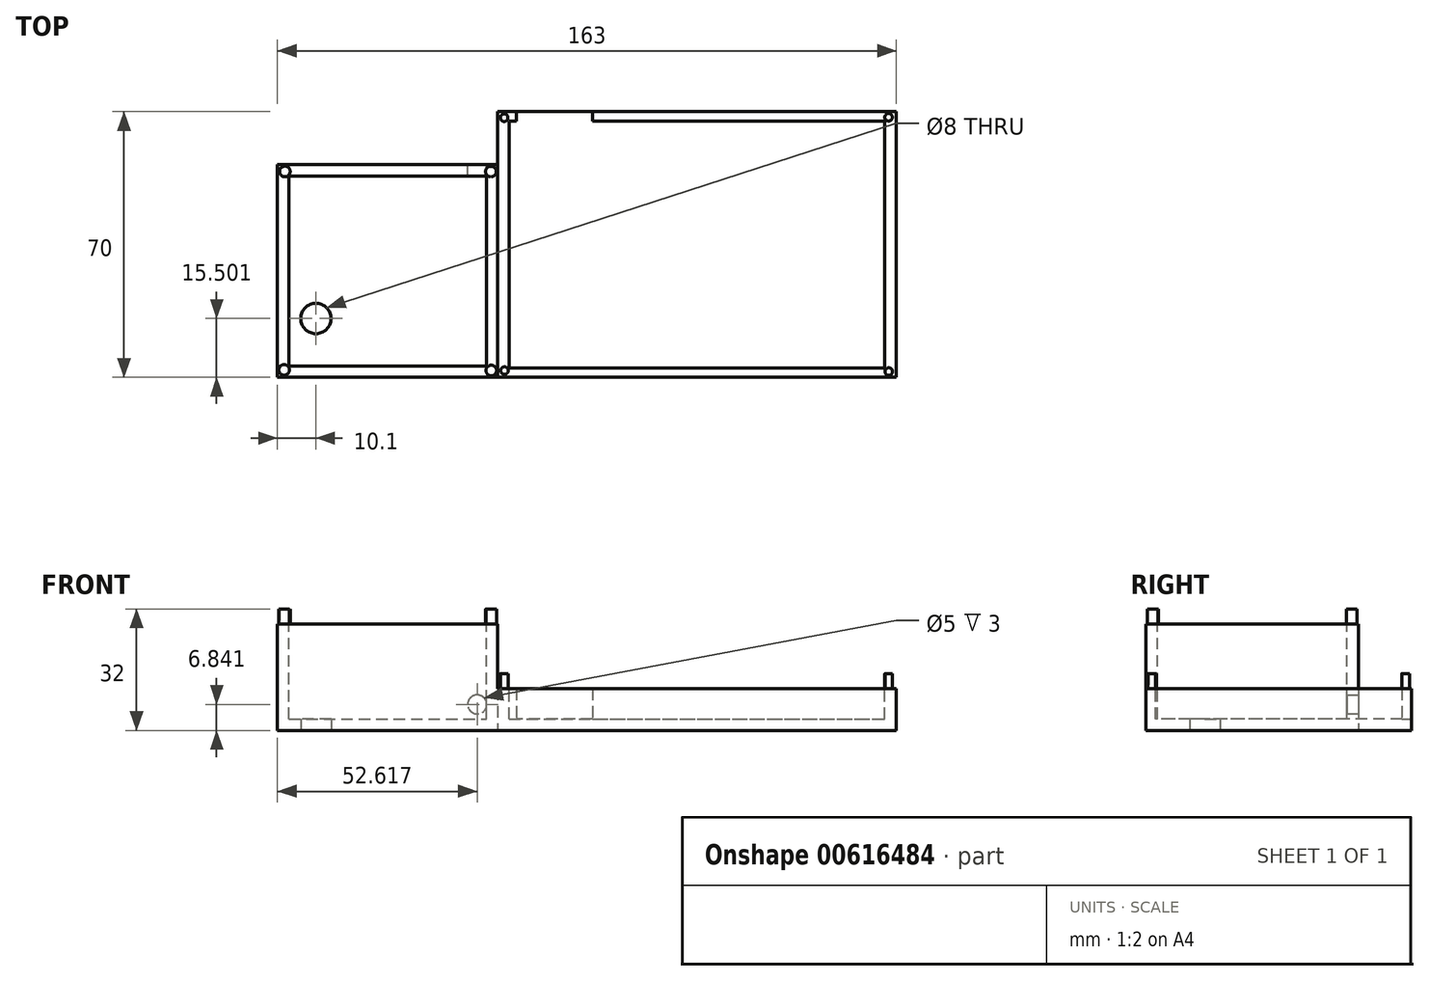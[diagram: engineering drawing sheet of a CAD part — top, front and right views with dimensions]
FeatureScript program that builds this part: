
annotation { "Feature Type Name" : "Feature", "Feature Type Description" : "" }
export const myFeature = defineFeature(function(context is Context, id is Id, definition is map)
    precondition{}
    {
        {
            var Q0;
            Q0=qCreatedBy(makeId("Top.planeOp"),FACE);
            var sketch = newSketch(context, id + "F0", { "sketchPlane" : qUnion([Q0])});
            skLineSegment(sketch, "E0.bottom", {"start": v(-52.5, 35) * mm, "end": v(52.5, 35) * mm});
            skLineSegment(sketch, "E0.top", {"start": v(-52.5, -35) * mm, "end": v(52.5, -35) * mm});
            skLineSegment(sketch, "E0.left", {"start": v(-52.5, 35) * mm, "end": v(-52.5, -35) * mm});
            skLineSegment(sketch, "E0.right", {"start": v(52.5, 35) * mm, "end": v(52.5, -35) * mm});
            skPoint(sketch, "E0.middle", {"position": v(0, 0) * mm});
            skSolve(sketch);
        }
        {
            var Q0;
            Q0=qCreatedBy(makeId("Top.planeOp"),FACE);
            var sketch = newSketch(context, id + "F1", { "sketchPlane" : qUnion([Q0])});
            skLineSegment(sketch, "E1.bottom", {"start": v(-52.5, 21) * mm, "end": v(-110.5, 21) * mm});
            skLineSegment(sketch, "E1.top", {"start": v(-52.5, -35) * mm, "end": v(-110.5, -35) * mm});
            skLineSegment(sketch, "E1.left", {"start": v(-52.5, 21) * mm, "end": v(-52.5, -35) * mm});
            skLineSegment(sketch, "E1.right", {"start": v(-110.5, 21) * mm, "end": v(-110.5, -35) * mm});
            skSolve(sketch);
        }
        {
            var Q0;
            Q0=makeQuery(id+"F1.imprint","IMPRINT",FACE,{"disambiguationData":[TD([[makeQuery(id+"F1.imprint","IMPRINT",EDGE,{"derivedFrom":sQuery(id+"F1.wireOp",EDGE,"E1.bottom")}),1.0]])]});
            var Q1;
            Q1=makeQuery(id+"F0.imprint","IMPRINT",FACE,{"disambiguationData":[TD([[makeQuery(id+"F0.imprint","IMPRINT",EDGE,{"derivedFrom":sQuery(id+"F0.wireOp",EDGE,"E0.bottom")}),-1.0]])]});
            extrude(context, id + "F2", {"entities" : qUnion([Q0, Q1]), "depth" : 11 * mm, "offsetDistance" : 25 * mm});
        }
        {
            var Q0;
            Q0=makeQuery(id+"F2.opExtrude","CAP_FACE",FACE,{"disambiguationData":[OSD([sQuery(id+"F0.wireOp",EDGE,"E0.bottom"),sQuery(id+"F0.wireOp",EDGE,"E0.top"),sQuery(id+"F0.wireOp",EDGE,"E0.left"),sQuery(id+"F0.wireOp",EDGE,"E0.right")])],"isStart":false});
            var sketch = newSketch(context, id + "F3", { "sketchPlane" : qUnion([Q0])});
            skLineSegment(sketch, "E2.bottom", {"start": v(-49.5, 32.5) * mm, "end": v(49.5, 32.5) * mm});
            skLineSegment(sketch, "E2.top", {"start": v(-49.5, -32.5) * mm, "end": v(49.5, -32.5) * mm});
            skLineSegment(sketch, "E2.left", {"start": v(-49.5, 32.5) * mm, "end": v(-49.5, -32.5) * mm});
            skLineSegment(sketch, "E2.right", {"start": v(49.5, 32.5) * mm, "end": v(49.5, -32.5) * mm});
            skPoint(sketch, "E2.middle", {"position": v(0, 0) * mm});
            skSolve(sketch);
        }
        {
            var Q0;
            Q0=makeQuery(id+"F3.imprint","IMPRINT",FACE,{"disambiguationData":[TD([[makeQuery(id+"F3.imprint","IMPRINT",EDGE,{"derivedFrom":sQuery(id+"F3.wireOp",EDGE,"E2.bottom")}),-1.0]])]});
            extrude(context, id + "F4", {"entities" : qUnion([Q0]), "operationType" : NewBodyOperationType.REMOVE, "oppositeDirection" : true, "depth" : 8 * mm, "offsetDistance" : 25 * mm});
        }
        {
            var Q0;
            Q0=makeQuery(id+"F2.opExtrude","SWEPT_FACE",FACE,{"disambiguationData":[OSD([sQuery(id+"F0.wireOp",EDGE,"E0.bottom")])]});
            var sketch = newSketch(context, id + "F5", { "sketchPlane" : qUnion([Q0])});
            skLineSegment(sketch, "E3.bottom", {"start": v(27.5, 11) * mm, "end": v(47.5, 11) * mm});
            skLineSegment(sketch, "E3.top", {"start": v(27.5, 3) * mm, "end": v(47.5, 3) * mm});
            skLineSegment(sketch, "E3.left", {"start": v(27.5, 11) * mm, "end": v(27.5, 3) * mm});
            skLineSegment(sketch, "E3.right", {"start": v(47.5, 11) * mm, "end": v(47.5, 3) * mm});
            skSolve(sketch);
        }
        {
            var Q0;
            Q0=makeQuery(id+"F5.imprint","IMPRINT",FACE,{"disambiguationData":[TD([[makeQuery(id+"F5.imprint","IMPRINT",EDGE,{"derivedFrom":sQuery(id+"F5.wireOp",EDGE,"E3.bottom")}),1.0]])]});
            extrude(context, id + "F6", {"entities" : qUnion([Q0]), "operationType" : NewBodyOperationType.REMOVE, "oppositeDirection" : true, "depth" : 2.5 * mm, "offsetDistance" : 25 * mm});
        }
        {
            var Q0;
            Q0=makeQuery(id+"F2.opExtrude","CAP_FACE",FACE,{"disambiguationData":[OSD([sQuery(id+"F1.wireOp",EDGE,"E1.bottom"),sQuery(id+"F1.wireOp",EDGE,"E1.top"),sQuery(id+"F1.wireOp",EDGE,"E1.left"),sQuery(id+"F1.wireOp",EDGE,"E1.right")])],"isStart":false});
            var sketch = newSketch(context, id + "F7", { "sketchPlane" : qUnion([Q0])});
            skLineSegment(sketch, "E4.bottom", {"start": v(-107.5, 18) * mm, "end": v(-55.5, 18) * mm});
            skLineSegment(sketch, "E4.top", {"start": v(-107.5, -32) * mm, "end": v(-55.5, -32) * mm});
            skLineSegment(sketch, "E4.left", {"start": v(-107.5, 18) * mm, "end": v(-107.5, -32) * mm});
            skLineSegment(sketch, "E4.right", {"start": v(-55.5, 18) * mm, "end": v(-55.5, -32) * mm});
            skSolve(sketch);
        }
        {
            var Q0;
            Q0=makeQuery(id+"F7.imprint","IMPRINT",FACE,{"disambiguationData":[TD([[makeQuery(id+"F7.imprint","IMPRINT",EDGE,{"derivedFrom":sQuery(id+"F7.wireOp",EDGE,"E4.bottom")}),-1.0]])]});
            extrude(context, id + "F8", {"entities" : qUnion([Q0]), "operationType" : NewBodyOperationType.REMOVE, "oppositeDirection" : true, "depth" : 8 * mm, "offsetDistance" : 25 * mm});
        }
        {
            var Q0;
            Q0=makeQuery(id+"F2.opExtrude","CAP_FACE",FACE,{"disambiguationData":[OSD([sQuery(id+"F1.wireOp",EDGE,"E1.bottom"),sQuery(id+"F1.wireOp",EDGE,"E1.top"),sQuery(id+"F1.wireOp",EDGE,"E1.left"),sQuery(id+"F1.wireOp",EDGE,"E1.right")])],"isStart":true});
            var sketch = newSketch(context, id + "F9", { "sketchPlane" : qUnion([Q0])});
            skCircle(sketch, "E5", {"center": v(-100.4, 19.5) * mm, "radius": 4 * mm});
            skSolve(sketch);
        }
        {
            var Q0;
            Q0=makeQuery(id+"F9.imprint","IMPRINT",FACE,{"disambiguationData":[TD([[makeQuery(id+"F9.imprint","IMPRINT",EDGE,{"derivedFrom":sQuery(id+"F9.wireOp",EDGE,"E5")}),1.0]])]});
            extrude(context, id + "F10", {"entities" : qUnion([Q0]), "operationType" : NewBodyOperationType.REMOVE, "oppositeDirection" : true, "depth" : 4 * mm, "offsetDistance" : 25 * mm});
        }
        {
            var Q0;
            Q0=makeQuery(id+"F2.opExtrude","CAP_FACE",FACE,{"disambiguationData":[OSD([sQuery(id+"F1.wireOp",EDGE,"E1.bottom"),sQuery(id+"F1.wireOp",EDGE,"E1.top"),sQuery(id+"F1.wireOp",EDGE,"E1.left"),sQuery(id+"F1.wireOp",EDGE,"E1.right")])],"isStart":false});
            extrude(context, id + "F11", {"entities" : qUnion([Q0]), "operationType" : NewBodyOperationType.ADD, "depth" : 17 * mm, "offsetDistance" : 25 * mm});
        }
        {
            var Q0;
            {var subQ0=sQuery(id+"F1.wireOp",EDGE,"E1.bottom");Q0=makeQuery(id+"F11.boolean.opBoolean","MERGE",FACE,{"derivedFrom":[makeQuery(id+"F2.opExtrude","SWEPT_FACE",FACE,{"disambiguationData":[OSD([subQ0])]}),makeQuery(id+"F11.opExtrude","SWEPT_FACE",FACE,{"disambiguationData":[OSD([subQ0])]})]});}
            var sketch = newSketch(context, id + "F12", { "sketchPlane" : qUnion([Q0])});
            skCircle(sketch, "E6", {"center": v(57.88, 6.84) * mm, "radius": 2.5 * mm});
            skSolve(sketch);
        }
        {
            var Q0;
            Q0=makeQuery(id+"F12.imprint","IMPRINT",FACE,{"disambiguationData":[TD([[makeQuery(id+"F12.imprint","IMPRINT",EDGE,{"derivedFrom":sQuery(id+"F12.wireOp",EDGE,"E6")}),1.0]])]});
            extrude(context, id + "F13", {"entities" : qUnion([Q0]), "operationType" : NewBodyOperationType.REMOVE, "oppositeDirection" : true, "depth" : 3 * mm, "offsetDistance" : 25 * mm});
        }
        {
            var Q0;
            Q0=makeQuery(id+"F11.opExtrude","CAP_FACE",FACE,{"disambiguationData":[OSD([sQuery(id+"F1.wireOp",EDGE,"E1.bottom"),sQuery(id+"F1.wireOp",EDGE,"E1.top"),sQuery(id+"F1.wireOp",EDGE,"E1.left"),sQuery(id+"F1.wireOp",EDGE,"E1.right")])],"isStart":false});
            var sketch = newSketch(context, id + "F14", { "sketchPlane" : qUnion([Q0])});
            skCircle(sketch, "E7", {"center": v(-108.57, 19.23) * mm, "radius": 1.4 * mm});
            skSolve(sketch);
        }
        {
            var Q0;
            Q0=makeQuery(id+"F14.imprint","IMPRINT",FACE,{"disambiguationData":[TD([[makeQuery(id+"F14.imprint","IMPRINT",EDGE,{"derivedFrom":sQuery(id+"F14.wireOp",EDGE,"E7")}),1.0]])]});
            extrude(context, id + "F15", {"entities" : qUnion([Q0]), "operationType" : NewBodyOperationType.ADD, "depth" : 4 * mm, "offsetDistance" : 25 * mm});
        }
        {
            var Q0;
            Q0=makeQuery(id+"F11.opExtrude","CAP_FACE",FACE,{"disambiguationData":[OSD([sQuery(id+"F1.wireOp",EDGE,"E1.bottom"),sQuery(id+"F1.wireOp",EDGE,"E1.top"),sQuery(id+"F1.wireOp",EDGE,"E1.left"),sQuery(id+"F1.wireOp",EDGE,"E1.right")])],"isStart":false});
            var sketch = newSketch(context, id + "F16", { "sketchPlane" : qUnion([Q0])});
            skCircle(sketch, "E8", {"center": v(-108.75, -33.04) * mm, "radius": 1.4 * mm});
            skCircle(sketch, "E9", {"center": v(-54.2, -33.2) * mm, "radius": 1.4 * mm});
            skCircle(sketch, "E10", {"center": v(-54.29, 19.2) * mm, "radius": 1.4 * mm});
            skSolve(sketch);
        }
        {
            var Q0;
            Q0=makeQuery(id+"F16.imprint","IMPRINT",FACE,{"disambiguationData":[TD([[makeQuery(id+"F16.imprint","IMPRINT",EDGE,{"derivedFrom":sQuery(id+"F16.wireOp",EDGE,"E8")}),1.0]])]});
            var Q1;
            Q1=makeQuery(id+"F16.imprint","IMPRINT",FACE,{"disambiguationData":[TD([[makeQuery(id+"F16.imprint","IMPRINT",EDGE,{"derivedFrom":sQuery(id+"F16.wireOp",EDGE,"E9")}),1.0]])]});
            var Q2;
            Q2=makeQuery(id+"F16.imprint","IMPRINT",FACE,{"disambiguationData":[TD([[makeQuery(id+"F16.imprint","IMPRINT",EDGE,{"derivedFrom":sQuery(id+"F16.wireOp",EDGE,"E10")}),1.0]])]});
            extrude(context, id + "F17", {"entities" : qUnion([Q0, Q1, Q2]), "operationType" : NewBodyOperationType.ADD, "depth" : 4 * mm, "offsetDistance" : 25 * mm});
        }
        {
            var Q0;
            Q0=makeQuery(id+"F2.opExtrude","CAP_FACE",FACE,{"disambiguationData":[OSD([sQuery(id+"F0.wireOp",EDGE,"E0.bottom"),sQuery(id+"F0.wireOp",EDGE,"E0.top"),sQuery(id+"F0.wireOp",EDGE,"E0.left"),sQuery(id+"F0.wireOp",EDGE,"E0.right")])],"isStart":false});
            var sketch = newSketch(context, id + "F18", { "sketchPlane" : qUnion([Q0])});
            skCircle(sketch, "E11", {"center": v(-50.8, 33.39) * mm, "radius": 1 * mm});
            skCircle(sketch, "E12", {"center": v(-50.89, -33.38) * mm, "radius": 1 * mm});
            skCircle(sketch, "E13", {"center": v(50.92, 33.38) * mm, "radius": 1 * mm});
            skCircle(sketch, "E14", {"center": v(50.75, -33.4) * mm, "radius": 1 * mm});
            skSolve(sketch);
        }
        {
            var Q0;
            Q0=makeQuery(id+"F18.imprint","IMPRINT",FACE,{"disambiguationData":[TD([[makeQuery(id+"F18.imprint","IMPRINT",EDGE,{"derivedFrom":sQuery(id+"F18.wireOp",EDGE,"E11")}),1.0]])]});
            extrude(context, id + "F19", {"entities" : qUnion([Q0]), "operationType" : NewBodyOperationType.ADD, "depth" : 4 * mm, "offsetDistance" : 25 * mm});
        }
        {
            var Q0;
            Q0=makeQuery(id+"F2.opExtrude","CAP_FACE",FACE,{"disambiguationData":[OSD([sQuery(id+"F0.wireOp",EDGE,"E0.bottom"),sQuery(id+"F0.wireOp",EDGE,"E0.top"),sQuery(id+"F0.wireOp",EDGE,"E0.left"),sQuery(id+"F0.wireOp",EDGE,"E0.right")])],"isStart":false});
            var sketch = newSketch(context, id + "F20", { "sketchPlane" : qUnion([Q0])});
            skCircle(sketch, "E15", {"center": v(50.5, 33.5) * mm, "radius": 1 * mm});
            skSolve(sketch);
        }
        {
            var Q0;
            Q0=makeQuery(id+"F20.imprint","IMPRINT",FACE,{"disambiguationData":[TD([[makeQuery(id+"F20.imprint","IMPRINT",EDGE,{"derivedFrom":sQuery(id+"F20.wireOp",EDGE,"E15")}),1.0]])]});
            extrude(context, id + "F21", {"entities" : qUnion([Q0]), "operationType" : NewBodyOperationType.ADD, "depth" : 4 * mm, "offsetDistance" : 25 * mm});
        }
        {
            var Q0;
            Q0=makeQuery(id+"F2.opExtrude","CAP_FACE",FACE,{"disambiguationData":[OSD([sQuery(id+"F0.wireOp",EDGE,"E0.bottom"),sQuery(id+"F0.wireOp",EDGE,"E0.top"),sQuery(id+"F0.wireOp",EDGE,"E0.left"),sQuery(id+"F0.wireOp",EDGE,"E0.right")])],"isStart":false});
            var sketch = newSketch(context, id + "F22", { "sketchPlane" : qUnion([Q0])});
            skCircle(sketch, "E16", {"center": v(50.55, -33.47) * mm, "radius": 1 * mm});
            skSolve(sketch);
        }
        {
            var Q0;
            Q0=makeQuery(id+"F22.imprint","IMPRINT",FACE,{"disambiguationData":[TD([[makeQuery(id+"F22.imprint","IMPRINT",EDGE,{"derivedFrom":sQuery(id+"F22.wireOp",EDGE,"E16")}),1.0]])]});
            extrude(context, id + "F23", {"entities" : qUnion([Q0]), "operationType" : NewBodyOperationType.ADD, "depth" : 4 * mm, "offsetDistance" : 25 * mm});
        }
        {
            var Q0;
            Q0=makeQuery(id+"F2.opExtrude","CAP_FACE",FACE,{"disambiguationData":[OSD([sQuery(id+"F0.wireOp",EDGE,"E0.bottom"),sQuery(id+"F0.wireOp",EDGE,"E0.top"),sQuery(id+"F0.wireOp",EDGE,"E0.left"),sQuery(id+"F0.wireOp",EDGE,"E0.right")])],"isStart":false});
            var sketch = newSketch(context, id + "F24", { "sketchPlane" : qUnion([Q0])});
            skCircle(sketch, "E17", {"center": v(-50.7, -33.21) * mm, "radius": 1 * mm});
            skSolve(sketch);
        }
        {
            var Q0;
            Q0=makeQuery(id+"F24.imprint","IMPRINT",FACE,{"disambiguationData":[TD([[makeQuery(id+"F24.imprint","IMPRINT",EDGE,{"derivedFrom":sQuery(id+"F24.wireOp",EDGE,"E17")}),1.0]])]});
            extrude(context, id + "F25", {"entities" : qUnion([Q0]), "operationType" : NewBodyOperationType.ADD, "depth" : 4 * mm, "offsetDistance" : 25 * mm});
        }
    });
